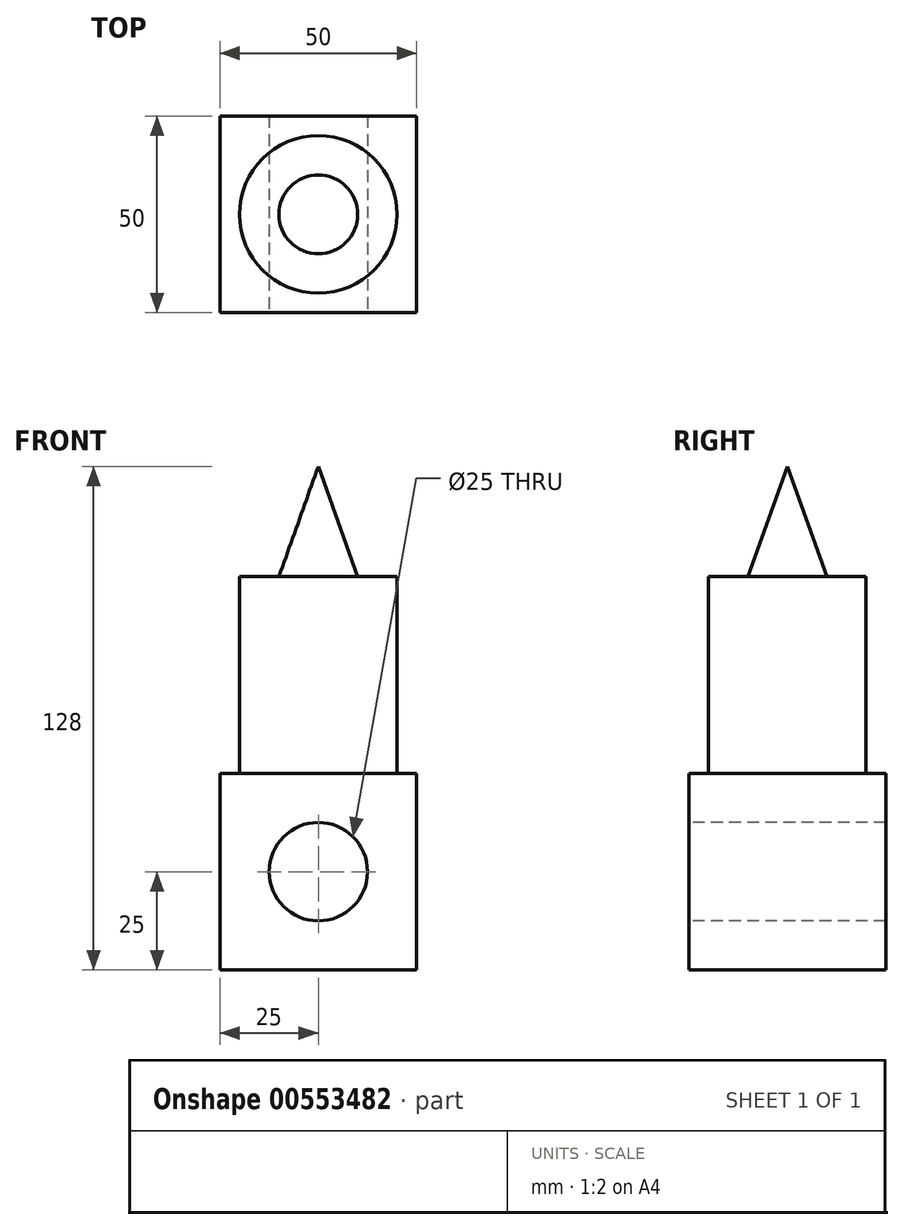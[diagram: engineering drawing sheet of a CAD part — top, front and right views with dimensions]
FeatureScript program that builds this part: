
annotation { "Feature Type Name" : "Feature", "Feature Type Description" : "" }
export const myFeature = defineFeature(function(context is Context, id is Id, definition is map)
    precondition{}
    {
        {
            var Q0;
            Q0=qCreatedBy(makeId("Front.planeOp"),FACE);
            var sketch = newSketch(context, id + "F0", { "sketchPlane" : qUnion([Q0])});
            skLineSegment(sketch, "E0.bottom", {"start": v(-25, 25) * mm, "end": v(25, 25) * mm});
            skLineSegment(sketch, "E0.top", {"start": v(-25, -25) * mm, "end": v(25, -25) * mm});
            skLineSegment(sketch, "E0.left", {"start": v(-25, 25) * mm, "end": v(-25, -25) * mm});
            skLineSegment(sketch, "E0.right", {"start": v(25, 25) * mm, "end": v(25, -25) * mm});
            skPoint(sketch, "E0.middle", {"position": v(0, 0) * mm});
            skSolve(sketch);
        }
        {
            var Q0;
            Q0=makeQuery(id+"F0.imprint","IMPRINT",FACE,{"disambiguationData":[TD([[makeQuery(id+"F0.imprint","IMPRINT",EDGE,{"derivedFrom":sQuery(id+"F0.wireOp",EDGE,"E0.bottom")}),-1.0]])]});
            extrude(context, id + "F1", {"entities" : qUnion([Q0]), "endBound" : BoundingType.SYMMETRIC, "depth" : 50 * mm, "offsetDistance" : 25 * mm});
        }
        {
            var Q0;
            Q0=makeQuery(id+"F1.opExtrude","CAP_FACE",FACE,{"disambiguationData":[OSD([sQuery(id+"F0.wireOp",EDGE,"E0.bottom"),sQuery(id+"F0.wireOp",EDGE,"E0.top"),sQuery(id+"F0.wireOp",EDGE,"E0.left"),sQuery(id+"F0.wireOp",EDGE,"E0.right")])],"isStart":false});
            var sketch = newSketch(context, id + "F2", { "sketchPlane" : qUnion([Q0])});
            skCircle(sketch, "E1", {"center": v(0, 0) * mm, "radius": 12.5 * mm});
            skSolve(sketch);
        }
        {
            var Q0;
            Q0=makeQuery(id+"F2.imprint","IMPRINT",FACE,{"disambiguationData":[TD([[makeQuery(id+"F2.imprint","IMPRINT",EDGE,{"derivedFrom":sQuery(id+"F2.wireOp",EDGE,"E1")}),1.0]])]});
            extrude(context, id + "F3", {"entities" : qUnion([Q0]), "operationType" : NewBodyOperationType.REMOVE, "oppositeDirection" : true, "depth" : 50 * mm, "offsetDistance" : 25 * mm});
        }
        {
            var Q0;
            Q0=makeQuery(id+"F1.opExtrude","SWEPT_FACE",FACE,{"disambiguationData":[OSD([sQuery(id+"F0.wireOp",EDGE,"E0.bottom")])]});
            var sketch = newSketch(context, id + "F4", { "sketchPlane" : qUnion([Q0])});
            skCircle(sketch, "E2", {"center": v(0, 0) * mm, "radius": 20 * mm});
            skSolve(sketch);
        }
        {
            var Q0;
            Q0=makeQuery(id+"F4.imprint","IMPRINT",FACE,{"disambiguationData":[TD([[makeQuery(id+"F4.imprint","IMPRINT",EDGE,{"derivedFrom":sQuery(id+"F4.wireOp",EDGE,"E2")}),1.0]])]});
            extrude(context, id + "F5", {"entities" : qUnion([Q0]), "operationType" : NewBodyOperationType.ADD, "depth" : 50 * mm, "offsetDistance" : 25 * mm});
        }
        {
            var Q0;
            Q0=qCreatedBy(makeId("Front.planeOp"),FACE);
            var sketch = newSketch(context, id + "F6", { "sketchPlane" : qUnion([Q0])});
            skLineSegment(sketch, "E3", {"start": v(0, 75) * mm, "end": v(0, 103) * mm});
            skLineSegment(sketch, "E4", {"start": v(0, 75) * mm, "end": v(10, 75) * mm});
            skLineSegment(sketch, "E5", {"start": v(10, 75) * mm, "end": v(0, 103) * mm});
            skSolve(sketch);
        }
        {
            var Q0;
            Q0=makeQuery(id+"F6.imprint","IMPRINT",FACE,{"disambiguationData":[TD([[makeQuery(id+"F6.imprint","IMPRINT",EDGE,{"derivedFrom":sQuery(id+"F6.wireOp",EDGE,"E3")}),-1.0]])]});
            var Q1;
            Q1=sQuery(id+"F6.wireOp",EDGE,"E3");
            revolve(context, id + "F7", {"operationType" : NewBodyOperationType.ADD, "entities" : qUnion([Q0]), "axis" : qUnion([Q1]), "revolveType" : RevolveType.FULL});
        }
    });
